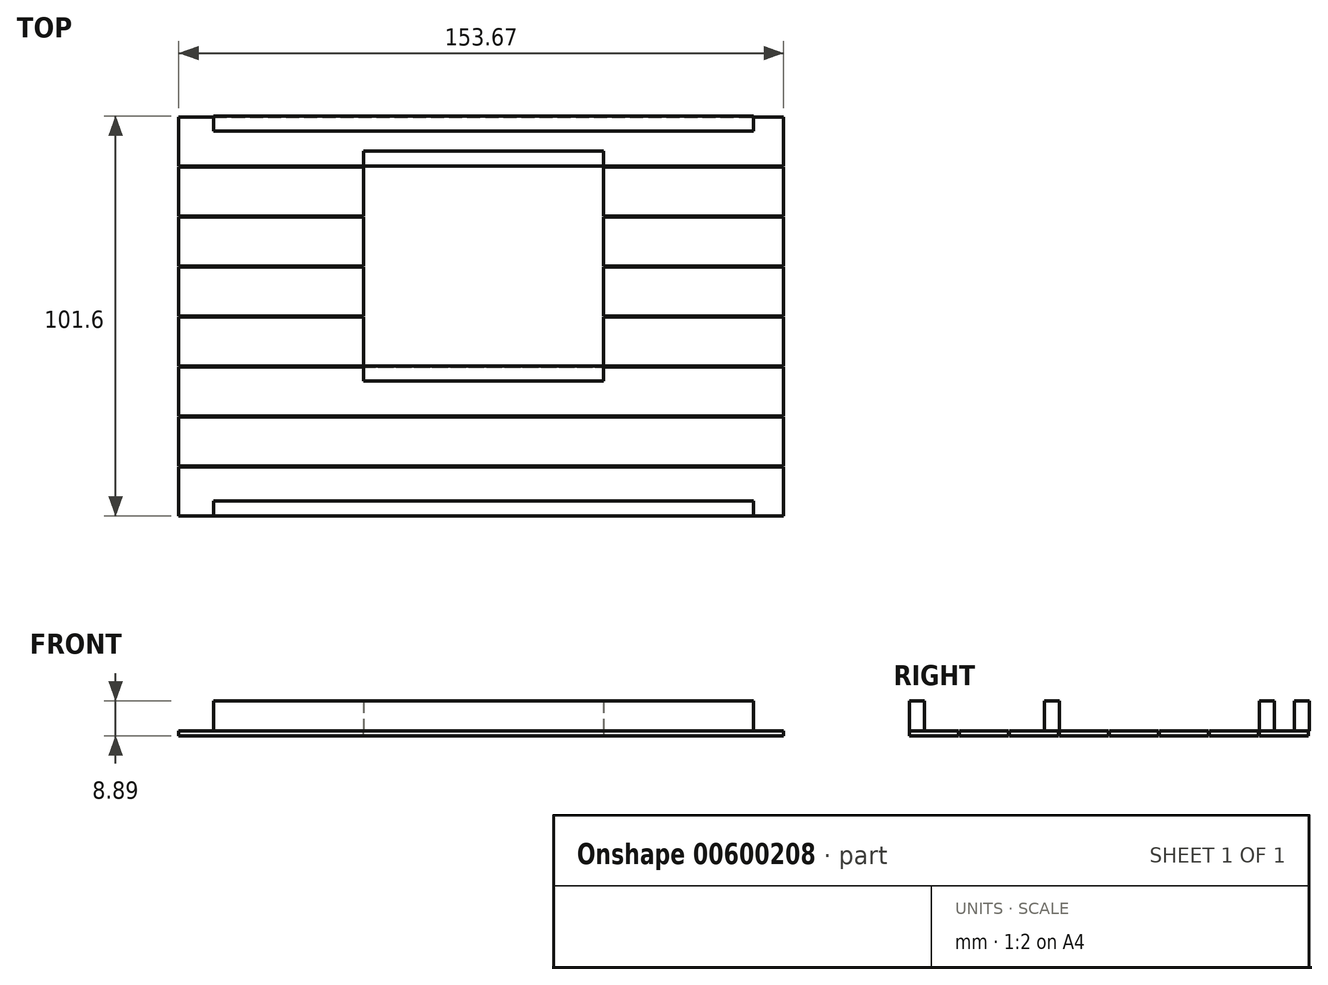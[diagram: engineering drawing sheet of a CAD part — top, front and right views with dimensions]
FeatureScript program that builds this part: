
annotation { "Feature Type Name" : "Feature", "Feature Type Description" : "" }
export const myFeature = defineFeature(function(context is Context, id is Id, definition is map)
    precondition{}
    {
        {
            var Q0;
            Q0=qCreatedBy(makeId("Top.planeOp"),FACE);
            var sketch = newSketch(context, id + "F0", { "sketchPlane" : qUnion([Q0])});
            skLineSegment(sketch, "E0.bottom", {"start": v(0, 0) * mm, "end": v(137.16, 0) * mm});
            skLineSegment(sketch, "E0.top", {"start": v(0, 3.81) * mm, "end": v(137.16, 3.81) * mm});
            skLineSegment(sketch, "E0.left", {"start": v(0, 0) * mm, "end": v(0, 3.81) * mm});
            skLineSegment(sketch, "E0.right", {"start": v(137.16, 0) * mm, "end": v(137.16, 3.81) * mm});
            skLineSegment(sketch, "E1.bottom", {"start": v(0, 3.81) * mm, "end": v(3.8, 3.81) * mm});
            skLineSegment(sketch, "E1.top", {"start": v(0, 97.8) * mm, "end": v(3.8, 97.8) * mm});
            skLineSegment(sketch, "E1.left", {"start": v(0, 3.81) * mm, "end": v(0, 97.8) * mm});
            skLineSegment(sketch, "E1.right", {"start": v(3.8, 3.81) * mm, "end": v(3.8, 97.8) * mm});
            skLineSegment(sketch, "E2.bottom", {"start": v(0, 97.8) * mm, "end": v(137.16, 97.8) * mm});
            skLineSegment(sketch, "E2.top", {"start": v(0, 101.6) * mm, "end": v(137.16, 101.6) * mm});
            skLineSegment(sketch, "E2.left", {"start": v(0, 97.8) * mm, "end": v(0, 101.6) * mm});
            skLineSegment(sketch, "E2.right", {"start": v(137.16, 97.8) * mm, "end": v(137.16, 101.6) * mm});
            skLineSegment(sketch, "E3.bottom", {"start": v(137.16, 3.81) * mm, "end": v(133.35, 3.81) * mm});
            skLineSegment(sketch, "E3.top", {"start": v(137.16, 97.8) * mm, "end": v(133.35, 97.8) * mm});
            skLineSegment(sketch, "E3.left", {"start": v(137.16, 3.81) * mm, "end": v(137.16, 97.8) * mm});
            skLineSegment(sketch, "E3.right", {"start": v(133.35, 3.81) * mm, "end": v(133.35, 97.8) * mm});
            skLineSegment(sketch, "E4.bottom", {"start": v(34.29, 97.8) * mm, "end": v(38.1, 97.8) * mm});
            skLineSegment(sketch, "E4.top", {"start": v(34.29, 3.81) * mm, "end": v(38.1, 3.81) * mm});
            skLineSegment(sketch, "E4.left", {"start": v(34.29, 97.8) * mm, "end": v(34.29, 3.81) * mm});
            skLineSegment(sketch, "E4.right", {"start": v(38.1, 97.8) * mm, "end": v(38.1, 3.81) * mm});
            skLineSegment(sketch, "E5.bottom", {"start": v(99.06, 97.8) * mm, "end": v(102.87, 97.8) * mm});
            skLineSegment(sketch, "E5.top", {"start": v(99.06, 3.81) * mm, "end": v(102.87, 3.81) * mm});
            skLineSegment(sketch, "E5.left", {"start": v(99.06, 97.8) * mm, "end": v(99.06, 3.81) * mm});
            skLineSegment(sketch, "E5.right", {"start": v(102.87, 97.8) * mm, "end": v(102.87, 3.81) * mm});
            skLineSegment(sketch, "E6.bottom", {"start": v(38.1, 92.7) * mm, "end": v(99.06, 92.7) * mm});
            skLineSegment(sketch, "E6.top", {"start": v(38.1, 88.9) * mm, "end": v(99.06, 88.9) * mm});
            skLineSegment(sketch, "E6.left", {"start": v(38.1, 92.7) * mm, "end": v(38.1, 88.9) * mm});
            skLineSegment(sketch, "E6.right", {"start": v(99.06, 92.7) * mm, "end": v(99.06, 88.9) * mm});
            skLineSegment(sketch, "E7.bottom", {"start": v(38.1, 38.1) * mm, "end": v(99.06, 38.1) * mm});
            skLineSegment(sketch, "E7.top", {"start": v(38.1, 34.3) * mm, "end": v(99.06, 34.3) * mm});
            skLineSegment(sketch, "E7.left", {"start": v(38.1, 38.1) * mm, "end": v(38.1, 34.3) * mm});
            skLineSegment(sketch, "E7.right", {"start": v(99.06, 38.1) * mm, "end": v(99.06, 34.3) * mm});
            skSolve(sketch);
        }
        {
            var Q0;
            Q0=makeQuery(id+"F0.imprint","IMPRINT",FACE,{"disambiguationData":[TD([[makeQuery(id+"F0.imprint","IMPRINT",EDGE,{"derivedFrom":sQuery(id+"F0.wireOp",EDGE,"E2.top")}),-1.0]])]});
            var Q1;
            {var subQ1=sQuery(id+"F0.wireOp",EDGE,"E4.bottom");Q1=makeQuery(id+"F0.imprint","IMPRINT",FACE,{"disambiguationData":[TD([[makeQuery(id+"F0.imprint","IMPRINT",EDGE,{"derivedFrom":subQ1}),-1.0]])]});}
            var Q2;
            Q2=makeQuery(id+"F0.imprint","IMPRINT",FACE,{"disambiguationData":[TD([[makeQuery(id+"F0.imprint","IMPRINT",EDGE,{"derivedFrom":sQuery(id+"F0.wireOp",EDGE,"E6.bottom")}),-1.0]])]});
            var Q3;
            {var subQ3=sQuery(id+"F0.wireOp",EDGE,"E5.bottom");Q3=makeQuery(id+"F0.imprint","IMPRINT",FACE,{"disambiguationData":[TD([[makeQuery(id+"F0.imprint","IMPRINT",EDGE,{"derivedFrom":subQ3}),-1.0]])]});}
            var Q4;
            Q4=makeQuery(id+"F0.imprint","IMPRINT",FACE,{"disambiguationData":[TD([[makeQuery(id+"F0.imprint","IMPRINT",EDGE,{"derivedFrom":sQuery(id+"F0.wireOp",EDGE,"E3.bottom")}),-1.0]])]});
            var Q5;
            Q5=makeQuery(id+"F0.imprint","IMPRINT",FACE,{"disambiguationData":[TD([[makeQuery(id+"F0.imprint","IMPRINT",EDGE,{"derivedFrom":sQuery(id+"F0.wireOp",EDGE,"E7.bottom")}),-1.0]])]});
            var Q6;
            Q6=makeQuery(id+"F0.imprint","IMPRINT",FACE,{"disambiguationData":[TD([[makeQuery(id+"F0.imprint","IMPRINT",EDGE,{"derivedFrom":sQuery(id+"F0.wireOp",EDGE,"E1.bottom")}),1.0]])]});
            var Q7;
            Q7=makeQuery(id+"F0.imprint","IMPRINT",FACE,{"disambiguationData":[TD([[makeQuery(id+"F0.imprint","IMPRINT",EDGE,{"derivedFrom":sQuery(id+"F0.wireOp",EDGE,"E0.bottom")}),1.0]])]});
            extrude(context, id + "F1", {"entities" : qUnion([Q0, Q1, Q2, Q3, Q4, Q5, Q6, Q7]), "depth" : 7.62 * mm, "offsetDistance" : 25.4 * mm});
        }
        {
            var Q0;
            Q0=qCreatedBy(makeId("Top.planeOp"),FACE);
            var sketch = newSketch(context, id + "F2", { "sketchPlane" : qUnion([Q0])});
            skLineSegment(sketch, "E8.bottom", {"start": v(-8.9, 0) * mm, "end": v(144.78, 0) * mm});
            skLineSegment(sketch, "E8.top", {"start": v(-8.9, 12.45) * mm, "end": v(144.78, 12.45) * mm});
            skLineSegment(sketch, "E8.left", {"start": v(-8.9, 0) * mm, "end": v(-8.9, 12.45) * mm});
            skLineSegment(sketch, "E8.right", {"start": v(144.78, 0) * mm, "end": v(144.78, 12.45) * mm});
            skLineSegment(sketch, "E9.0.1.0", {"start": v(-8.9, 12.7) * mm, "end": v(144.78, 12.7) * mm});
            skLineSegment(sketch, "E9.0.1.1", {"start": v(-8.9, 12.7) * mm, "end": v(-8.9, 25.15) * mm});
            skLineSegment(sketch, "E9.0.1.2", {"start": v(-8.9, 25.15) * mm, "end": v(144.78, 25.15) * mm});
            skLineSegment(sketch, "E9.0.1.3", {"start": v(144.78, 12.7) * mm, "end": v(144.78, 25.15) * mm});
            skLineSegment(sketch, "E9.0.2.0", {"start": v(-8.9, 25.4) * mm, "end": v(144.78, 25.4) * mm});
            skLineSegment(sketch, "E9.0.2.1", {"start": v(-8.9, 25.4) * mm, "end": v(-8.9, 37.85) * mm});
            skLineSegment(sketch, "E9.0.2.2", {"start": v(-8.9, 37.85) * mm, "end": v(144.78, 37.85) * mm});
            skLineSegment(sketch, "E9.0.2.3", {"start": v(144.78, 25.4) * mm, "end": v(144.78, 37.85) * mm});
            skLineSegment(sketch, "E9.0.3.0", {"start": v(-8.9, 38.1) * mm, "end": v(144.78, 38.1) * mm});
            skLineSegment(sketch, "E9.0.3.1", {"start": v(-8.9, 38.1) * mm, "end": v(-8.9, 50.55) * mm});
            skLineSegment(sketch, "E9.0.3.2", {"start": v(-8.9, 50.55) * mm, "end": v(144.78, 50.55) * mm});
            skLineSegment(sketch, "E9.0.3.3", {"start": v(144.78, 38.1) * mm, "end": v(144.78, 50.55) * mm});
            skLineSegment(sketch, "E9.0.4.0", {"start": v(-8.9, 50.8) * mm, "end": v(144.78, 50.8) * mm});
            skLineSegment(sketch, "E9.0.4.1", {"start": v(-8.9, 50.8) * mm, "end": v(-8.9, 63.25) * mm});
            skLineSegment(sketch, "E9.0.4.2", {"start": v(-8.9, 63.25) * mm, "end": v(144.78, 63.25) * mm});
            skLineSegment(sketch, "E9.0.4.3", {"start": v(144.78, 50.8) * mm, "end": v(144.78, 63.25) * mm});
            skLineSegment(sketch, "E9.0.5.0", {"start": v(-8.9, 63.5) * mm, "end": v(144.78, 63.5) * mm});
            skLineSegment(sketch, "E9.0.5.1", {"start": v(-8.9, 63.5) * mm, "end": v(-8.9, 75.95) * mm});
            skLineSegment(sketch, "E9.0.5.2", {"start": v(-8.9, 75.95) * mm, "end": v(144.78, 75.95) * mm});
            skLineSegment(sketch, "E9.0.5.3", {"start": v(144.78, 63.5) * mm, "end": v(144.78, 75.95) * mm});
            skLineSegment(sketch, "E9.direction1", {"start": v(-8.9, 0) * mm, "end": v(16.51, 0) * mm, "construction": true});
            skLineSegment(sketch, "E9.direction2", {"start": v(-8.9, 0) * mm, "end": v(-8.9, 12.7) * mm, "construction": true});
            skLineSegment(sketch, "E10.0.0.6", {"start": v(-8.9, 76.2) * mm, "end": v(144.78, 76.2) * mm});
            skLineSegment(sketch, "E10.3.0.6", {"start": v(-8.9, 76.2) * mm, "end": v(-8.9, 88.65) * mm});
            skLineSegment(sketch, "E10.6.0.6", {"start": v(-8.9, 88.65) * mm, "end": v(144.78, 88.65) * mm});
            skLineSegment(sketch, "E10.9.0.6", {"start": v(144.78, 76.2) * mm, "end": v(144.78, 88.65) * mm});
            skLineSegment(sketch, "E10.0.0.7", {"start": v(-8.9, 88.9) * mm, "end": v(144.78, 88.9) * mm});
            skLineSegment(sketch, "E10.3.0.7", {"start": v(-8.9, 88.9) * mm, "end": v(-8.9, 101.35) * mm});
            skLineSegment(sketch, "E10.6.0.7", {"start": v(-8.9, 101.35) * mm, "end": v(144.78, 101.35) * mm});
            skLineSegment(sketch, "E10.9.0.7", {"start": v(144.78, 88.9) * mm, "end": v(144.78, 101.35) * mm});
            skSolve(sketch);
        }
        {
            var Q0;
            Q0=makeQuery(id+"F2.imprint","IMPRINT",FACE,{"disambiguationData":[TD([[makeQuery(id+"F2.imprint","IMPRINT",EDGE,{"derivedFrom":sQuery(id+"F2.wireOp",EDGE,"E8.bottom")}),1.0]])]});
            var Q1;
            Q1=makeQuery(id+"F2.imprint","IMPRINT",FACE,{"disambiguationData":[TD([[makeQuery(id+"F2.imprint","IMPRINT",EDGE,{"derivedFrom":sQuery(id+"F2.wireOp",EDGE,"E9.0.1.0")}),1.0]])]});
            var Q2;
            Q2=makeQuery(id+"F2.imprint","IMPRINT",FACE,{"disambiguationData":[TD([[makeQuery(id+"F2.imprint","IMPRINT",EDGE,{"derivedFrom":sQuery(id+"F2.wireOp",EDGE,"E9.0.2.0")}),1.0]])]});
            var Q3;
            Q3=makeQuery(id+"F2.imprint","IMPRINT",FACE,{"disambiguationData":[TD([[makeQuery(id+"F2.imprint","IMPRINT",EDGE,{"derivedFrom":sQuery(id+"F2.wireOp",EDGE,"E9.0.3.0")}),1.0]])]});
            var Q4;
            Q4=makeQuery(id+"F2.imprint","IMPRINT",FACE,{"disambiguationData":[TD([[makeQuery(id+"F2.imprint","IMPRINT",EDGE,{"derivedFrom":sQuery(id+"F2.wireOp",EDGE,"E9.0.4.0")}),1.0]])]});
            var Q5;
            Q5=makeQuery(id+"F2.imprint","IMPRINT",FACE,{"disambiguationData":[TD([[makeQuery(id+"F2.imprint","IMPRINT",EDGE,{"derivedFrom":sQuery(id+"F2.wireOp",EDGE,"E9.0.5.0")}),1.0]])]});
            var Q6;
            Q6=makeQuery(id+"F2.imprint","IMPRINT",FACE,{"disambiguationData":[TD([[makeQuery(id+"F2.imprint","IMPRINT",EDGE,{"derivedFrom":sQuery(id+"F2.wireOp",EDGE,"E10.0.0.6")}),1.0]])]});
            var Q7;
            Q7=makeQuery(id+"F2.imprint","IMPRINT",FACE,{"disambiguationData":[TD([[makeQuery(id+"F2.imprint","IMPRINT",EDGE,{"derivedFrom":sQuery(id+"F2.wireOp",EDGE,"E10.0.0.7")}),1.0]])]});
            extrude(context, id + "F3", {"entities" : qUnion([Q0, Q1, Q2, Q3, Q4, Q5, Q6, Q7]), "oppositeDirection" : true, "depth" : 1.27 * mm, "offsetDistance" : 25.4 * mm});
        }
        {
            var Q0;
            {var subQ0=sQuery(id+"F0.wireOp",EDGE,"E6.top");Q0=makeQuery(id+"F0.imprint","IMPRINT",FACE,{"disambiguationData":[TD([[makeQuery(id+"F0.imprint","IMPRINT",EDGE,{"derivedFrom":subQ0}),-1.0]])]});}
            extrude(context, id + "F4", {"entities" : qUnion([Q0]), "operationType" : NewBodyOperationType.REMOVE, "oppositeDirection" : true, "depth" : 25.4 * mm, "offsetDistance" : 25.4 * mm});
        }
    });
